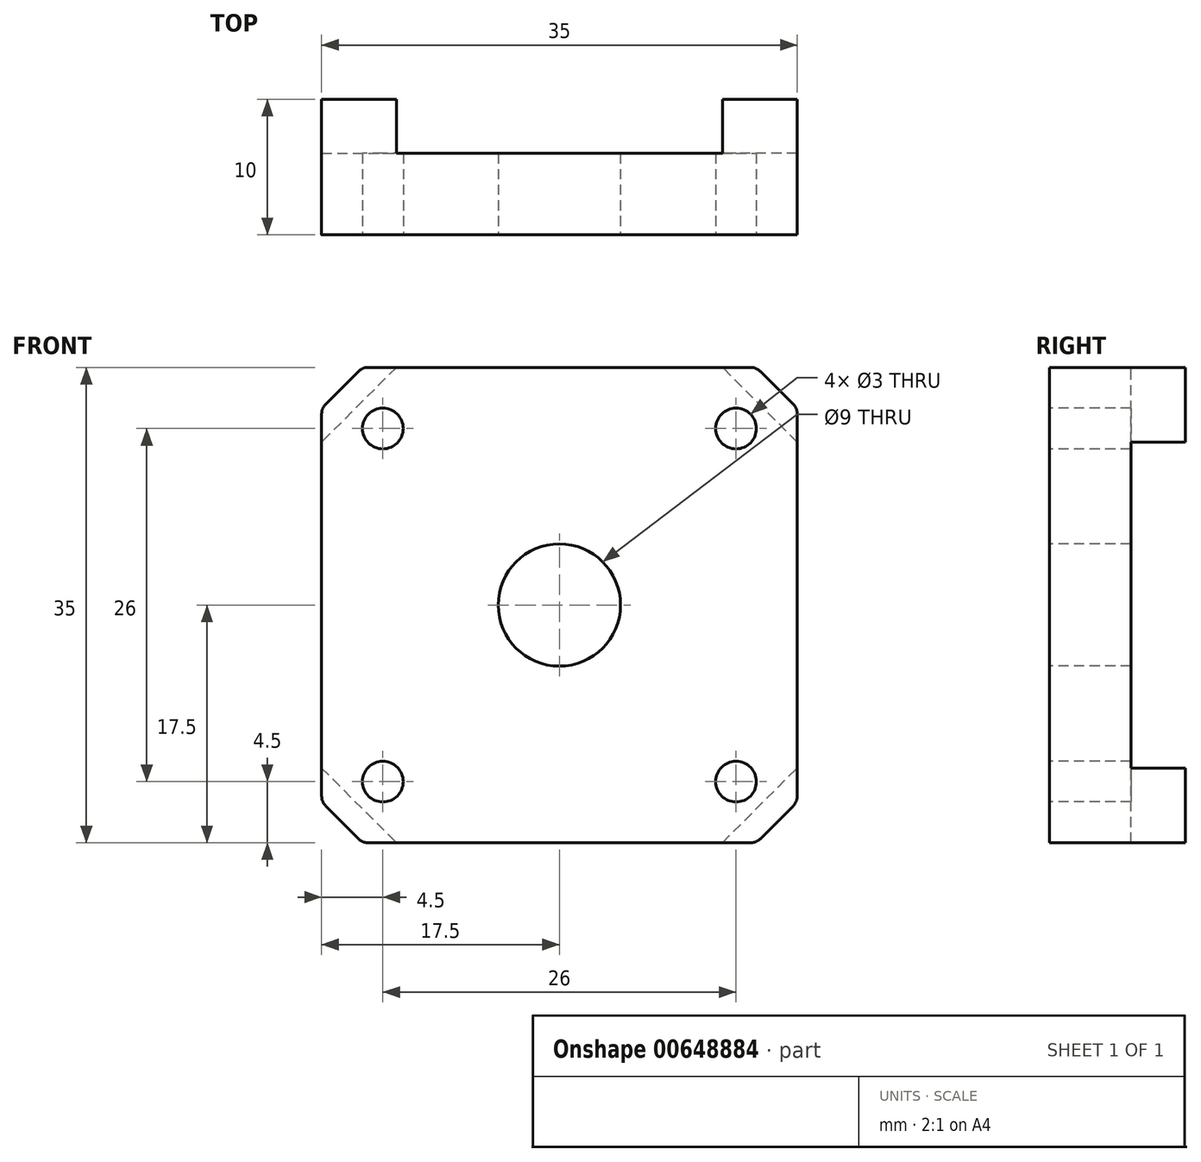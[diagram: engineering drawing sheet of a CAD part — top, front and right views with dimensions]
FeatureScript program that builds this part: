
annotation { "Feature Type Name" : "Feature", "Feature Type Description" : "" }
export const myFeature = defineFeature(function(context is Context, id is Id, definition is map)
    precondition{}
    {
        {
            var Q0;
            Q0=qCreatedBy(makeId("Front.planeOp"),FACE);
            var sketch = newSketch(context, id + "F0", { "sketchPlane" : qUnion([Q0])});
            skLineSegment(sketch, "E0.bottom", {"start": v(-17.5, 17.5) * mm, "end": v(17.5, 17.5) * mm});
            skLineSegment(sketch, "E0.top", {"start": v(-17.5, -17.5) * mm, "end": v(17.5, -17.5) * mm});
            skLineSegment(sketch, "E0.left", {"start": v(-17.5, 17.5) * mm, "end": v(-17.5, -17.5) * mm});
            skLineSegment(sketch, "E0.right", {"start": v(17.5, 17.5) * mm, "end": v(17.5, -17.5) * mm});
            skPoint(sketch, "E0.middle", {"position": v(0, 0) * mm});
            skSolve(sketch);
        }
        {
            var Q0;
            Q0=makeQuery(id+"F0.imprint","IMPRINT",FACE,{"disambiguationData":[TD([[makeQuery(id+"F0.imprint","IMPRINT",EDGE,{"derivedFrom":sQuery(id+"F0.wireOp",EDGE,"E0.bottom")}),-1.0]])]});
            extrude(context, id + "F1", {"entities" : qUnion([Q0]), "depth" : 10 * mm, "offsetDistance" : 25 * mm});
        }
        {
            var Q0;
            Q0=makeQuery(id+"F1.opExtrude","SWEPT_EDGE",EDGE,{"disambiguationData":[OSD([sQuery(id+"F0.wireOp",EDGE,"E0.bottom"),sQuery(id+"F0.wireOp",EDGE,"E0.left")])]});
            var Q1;
            Q1=makeQuery(id+"F1.opExtrude","SWEPT_EDGE",EDGE,{"disambiguationData":[OSD([sQuery(id+"F0.wireOp",EDGE,"E0.bottom"),sQuery(id+"F0.wireOp",EDGE,"E0.right")])]});
            var Q2;
            Q2=makeQuery(id+"F1.opExtrude","SWEPT_EDGE",EDGE,{"disambiguationData":[OSD([sQuery(id+"F0.wireOp",EDGE,"E0.top"),sQuery(id+"F0.wireOp",EDGE,"E0.right")])]});
            var Q3;
            Q3=makeQuery(id+"F1.opExtrude","SWEPT_EDGE",EDGE,{"disambiguationData":[OSD([sQuery(id+"F0.wireOp",EDGE,"E0.top"),sQuery(id+"F0.wireOp",EDGE,"E0.left")])]});
            chamfer(context, id + "F2", {"entities" : qUnion([Q0, Q1, Q2, Q3]), "width" : 3 * mm, "tangentPropagation" : true});
        }
        {
            var Q0;
            {var subQ0=sQuery(id+"F0.wireOp",EDGE,"E0.bottom");Q0=makeQuery(id+"F2.opChamfer","BLEND_EDGE",EDGE,{"blendedFrom":[makeQuery(id+"F1.opExtrude","SWEPT_EDGE",EDGE,{"disambiguationData":[OSD([subQ0,sQuery(id+"F0.wireOp",EDGE,"E0.left")])]}),makeQuery(id+"F1.opExtrude","SWEPT_FACE",FACE,{"disambiguationData":[OSD([subQ0])]})],"blendedInto":[makeQuery(id+"F1.opExtrude","SWEPT_FACE",FACE,{"disambiguationData":[OSD([subQ0])]})]});}
            var Q1;
            {var subQ0=sQuery(id+"F0.wireOp",EDGE,"E0.bottom");Q1=makeQuery(id+"F2.opChamfer","BLEND_EDGE",EDGE,{"blendedFrom":[makeQuery(id+"F1.opExtrude","SWEPT_EDGE",EDGE,{"disambiguationData":[OSD([subQ0,sQuery(id+"F0.wireOp",EDGE,"E0.right")])]}),makeQuery(id+"F1.opExtrude","SWEPT_FACE",FACE,{"disambiguationData":[OSD([subQ0])]})],"blendedInto":[makeQuery(id+"F1.opExtrude","SWEPT_FACE",FACE,{"disambiguationData":[OSD([subQ0])]})]});}
            var Q2;
            {var subQ0=sQuery(id+"F0.wireOp",EDGE,"E0.right");Q2=makeQuery(id+"F2.opChamfer","BLEND_EDGE",EDGE,{"blendedFrom":[makeQuery(id+"F1.opExtrude","SWEPT_EDGE",EDGE,{"disambiguationData":[OSD([sQuery(id+"F0.wireOp",EDGE,"E0.bottom"),subQ0])]}),makeQuery(id+"F1.opExtrude","SWEPT_FACE",FACE,{"disambiguationData":[OSD([subQ0])]})],"blendedInto":[makeQuery(id+"F1.opExtrude","SWEPT_FACE",FACE,{"disambiguationData":[OSD([subQ0])]})]});}
            var Q3;
            {var subQ0=sQuery(id+"F0.wireOp",EDGE,"E0.right");Q3=makeQuery(id+"F2.opChamfer","BLEND_EDGE",EDGE,{"blendedFrom":[makeQuery(id+"F1.opExtrude","SWEPT_EDGE",EDGE,{"disambiguationData":[OSD([sQuery(id+"F0.wireOp",EDGE,"E0.top"),subQ0])]}),makeQuery(id+"F1.opExtrude","SWEPT_FACE",FACE,{"disambiguationData":[OSD([subQ0])]})],"blendedInto":[makeQuery(id+"F1.opExtrude","SWEPT_FACE",FACE,{"disambiguationData":[OSD([subQ0])]})]});}
            var Q4;
            {var subQ0=sQuery(id+"F0.wireOp",EDGE,"E0.top");Q4=makeQuery(id+"F2.opChamfer","BLEND_EDGE",EDGE,{"blendedFrom":[makeQuery(id+"F1.opExtrude","SWEPT_EDGE",EDGE,{"disambiguationData":[OSD([subQ0,sQuery(id+"F0.wireOp",EDGE,"E0.right")])]}),makeQuery(id+"F1.opExtrude","SWEPT_FACE",FACE,{"disambiguationData":[OSD([subQ0])]})],"blendedInto":[makeQuery(id+"F1.opExtrude","SWEPT_FACE",FACE,{"disambiguationData":[OSD([subQ0])]})]});}
            var Q5;
            {var subQ0=sQuery(id+"F0.wireOp",EDGE,"E0.top");Q5=makeQuery(id+"F2.opChamfer","BLEND_EDGE",EDGE,{"blendedFrom":[makeQuery(id+"F1.opExtrude","SWEPT_EDGE",EDGE,{"disambiguationData":[OSD([subQ0,sQuery(id+"F0.wireOp",EDGE,"E0.left")])]}),makeQuery(id+"F1.opExtrude","SWEPT_FACE",FACE,{"disambiguationData":[OSD([subQ0])]})],"blendedInto":[makeQuery(id+"F1.opExtrude","SWEPT_FACE",FACE,{"disambiguationData":[OSD([subQ0])]})]});}
            var Q6;
            {var subQ0=sQuery(id+"F0.wireOp",EDGE,"E0.left");Q6=makeQuery(id+"F2.opChamfer","BLEND_EDGE",EDGE,{"blendedFrom":[makeQuery(id+"F1.opExtrude","SWEPT_EDGE",EDGE,{"disambiguationData":[OSD([sQuery(id+"F0.wireOp",EDGE,"E0.top"),subQ0])]}),makeQuery(id+"F1.opExtrude","SWEPT_FACE",FACE,{"disambiguationData":[OSD([subQ0])]})],"blendedInto":[makeQuery(id+"F1.opExtrude","SWEPT_FACE",FACE,{"disambiguationData":[OSD([subQ0])]})]});}
            var Q7;
            {var subQ0=sQuery(id+"F0.wireOp",EDGE,"E0.left");Q7=makeQuery(id+"F2.opChamfer","BLEND_EDGE",EDGE,{"blendedFrom":[makeQuery(id+"F1.opExtrude","SWEPT_EDGE",EDGE,{"disambiguationData":[OSD([sQuery(id+"F0.wireOp",EDGE,"E0.bottom"),subQ0])]}),makeQuery(id+"F1.opExtrude","SWEPT_FACE",FACE,{"disambiguationData":[OSD([subQ0])]})],"blendedInto":[makeQuery(id+"F1.opExtrude","SWEPT_FACE",FACE,{"disambiguationData":[OSD([subQ0])]})]});}
            fillet(context, id + "F3", {"entities" : qUnion([Q0, Q1, Q2, Q3, Q4, Q5, Q6, Q7]), "radius" : 1 * mm, "tangentPropagation" : true, "allowEdgeOverflow" : false});
        }
        {
            var Q0;
            Q0=makeQuery(id+"F1.opExtrude","CAP_FACE",FACE,{"disambiguationData":[OSD([sQuery(id+"F0.wireOp",EDGE,"E0.bottom"),sQuery(id+"F0.wireOp",EDGE,"E0.top"),sQuery(id+"F0.wireOp",EDGE,"E0.left"),sQuery(id+"F0.wireOp",EDGE,"E0.right")])],"isStart":false});
            var sketch = newSketch(context, id + "F4", { "sketchPlane" : qUnion([Q0])});
            skCircle(sketch, "E1", {"center": v(-13, 13) * mm, "radius": 1.5 * mm});
            skCircle(sketch, "E2.1.0", {"center": v(-13, -13) * mm, "radius": 1.5 * mm});
            skCircle(sketch, "E2.2.0", {"center": v(13, -13) * mm, "radius": 1.5 * mm});
            skCircle(sketch, "E2.3.0", {"center": v(13, 13) * mm, "radius": 1.5 * mm});
            skPoint(sketch, "E2.center", {"position": v(0, 0) * mm});
            skSolve(sketch);
        }
        {
            var Q0;
            Q0=qSketchRegion(id+"F4",true);
            extrude(context, id + "F5", {"entities" : qUnion([Q0]), "operationType" : NewBodyOperationType.REMOVE, "endBound" : BoundingType.THROUGH_ALL, "oppositeDirection" : true, "depth" : 25 * mm, "offsetDistance" : 25 * mm});
        }
        {
            var Q0;
            Q0=makeQuery(id+"F1.opExtrude","CAP_FACE",FACE,{"disambiguationData":[OSD([sQuery(id+"F0.wireOp",EDGE,"E0.bottom"),sQuery(id+"F0.wireOp",EDGE,"E0.top"),sQuery(id+"F0.wireOp",EDGE,"E0.left"),sQuery(id+"F0.wireOp",EDGE,"E0.right")])],"isStart":false});
            var sketch = newSketch(context, id + "F6", { "sketchPlane" : qUnion([Q0])});
            skCircle(sketch, "E3", {"center": v(0, 0) * mm, "radius": 4.5 * mm});
            skSolve(sketch);
        }
        {
            var Q0;
            Q0=makeQuery(id+"F6.imprint","IMPRINT",FACE,{"disambiguationData":[TD([[makeQuery(id+"F6.imprint","IMPRINT",EDGE,{"derivedFrom":sQuery(id+"F6.wireOp",EDGE,"E3")}),1.0]])]});
            extrude(context, id + "F7", {"entities" : qUnion([Q0]), "operationType" : NewBodyOperationType.REMOVE, "endBound" : BoundingType.THROUGH_ALL, "oppositeDirection" : true, "depth" : 25 * mm, "offsetDistance" : 25 * mm});
        }
        {
            var Q0;
            Q0=makeQuery(id+"F1.opExtrude","CAP_FACE",FACE,{"disambiguationData":[OSD([sQuery(id+"F0.wireOp",EDGE,"E0.bottom"),sQuery(id+"F0.wireOp",EDGE,"E0.top"),sQuery(id+"F0.wireOp",EDGE,"E0.left"),sQuery(id+"F0.wireOp",EDGE,"E0.right")])],"isStart":true});
            var sketch = newSketch(context, id + "F8", { "sketchPlane" : qUnion([Q0])});
            skLineSegment(sketch, "E4.bottom", {"start": v(-12, 17.5) * mm, "end": v(12, 17.5) * mm});
            skLineSegment(sketch, "E4.top", {"start": v(-12, -17.5) * mm, "end": v(12, -17.5) * mm});
            skLineSegment(sketch, "E4.left", {"start": v(-17.5, 12) * mm, "end": v(-17.5, -12) * mm});
            skLineSegment(sketch, "E4.right", {"start": v(17.5, 12) * mm, "end": v(17.5, -12) * mm});
            skPoint(sketch, "E4.middle", {"position": v(0, 0) * mm});
            skLineSegment(sketch, "E5", {"start": v(-17.5, 12) * mm, "end": v(-12, 17.5) * mm});
            skLineSegment(sketch, "E6.1.0", {"start": v(-12, -17.5) * mm, "end": v(-17.5, -12) * mm});
            skLineSegment(sketch, "E6.2.0", {"start": v(17.5, -12) * mm, "end": v(12, -17.5) * mm});
            skLineSegment(sketch, "E6.3.0", {"start": v(12, 17.5) * mm, "end": v(17.5, 12) * mm});
            skPoint(sketch, "E7.orphan", {"position": v(-17.5, 17.5) * mm});
            skPoint(sketch, "E8.orphan", {"position": v(-17.5, -17.5) * mm});
            skPoint(sketch, "E9.orphan", {"position": v(17.5, -17.5) * mm});
            skPoint(sketch, "E10.orphan", {"position": v(17.5, 17.5) * mm});
            skSolve(sketch);
        }
        {
            var Q0;
            Q0 = qSketchRegion(id + "F8", true);
            extrude(context, id + "F9", {"entities" : qUnion([Q0]), "operationType" : NewBodyOperationType.REMOVE, "oppositeDirection" : true, "depth" : 4 * mm, "offsetDistance" : 25 * mm});
        }
    });
